# Revit family: BVFC gran
name_source: partatom
category: Modelos genéricos
revit_build: Autodesk Revit 2017 (Build: 20160225_1515(x64)
units: mm (PartAtom-declared; Revit-internal decimal feet)

## family parameters
Compartido = No
Corte con vacíos al cargar = No
Cota de conector redondo = Diámetro de uso
Puede alojar armadura = No
Punto de cálculo de habitación = No
Se basa en plano de trabajo = No
Siempre vertical = Sí
Tipo de pieza = Normal

## types (4) — shared parameters
EspPeu = 3 mm  [stored 0.00984252 ft]
F = 30 mm  [stored 0.0984252 ft]
Fabricante = Casals Ventilació
N = 100 mm  [stored 0.328084 ft]
Q = 60 mm  [stored 0.19685 ft]
T = 52 mm
URL = www.casals.com
a = 10 mm  [stored 0.0328084 ft]
b = 26 mm
esp = 2 mm  [stored 0.00656168 ft]

## per-type parameters (varying)
| type | A | B | C | Dimensiones | E | G | H | K | M | O | P |
| BVFC 20/20 | 1551 mm | 1118 mm | 1406 mm  [stored 4.61286 ft] | 1406x1217,5x1697 | 611 mm | 1300 mm  [stored 4.26509 ft] | 1013 mm | 1697 mm  [stored 5.56759 ft] | 1295 mm | 101 mm  [stored 0.331365 ft] | 407 mm |
| BVFC 22/22 | 1801 mm | 1202 mm | 1499 mm  [stored 4.91798 ft] | 1499x1301,5x1997 | 697 mm | 1393 mm  [stored 4.57021 ft] | 1097 mm | 1997 mm | 1388 mm  [stored 4.55381 ft] | 99 mm  [stored 0.324803 ft] | 406 mm  [stored 1.33202 ft] |
| BVFC 25/25 | 1901 mm | 1327 mm | 1709 mm  [stored 5.60696 ft] | 1709x1426,5x2097 | 793 mm  [stored 2.60171 ft] | 1603 mm  [stored 5.25919 ft] | 1222 mm  [stored 4.00919 ft] | 2048 mm | 1598 mm  [stored 5.24278 ft] | 101 mm  [stored 0.331365 ft] | 433 mm |
| BVFC 30/28 | 2108 mm | 1557 mm | 1906 mm | 1906x1656,5x2304 | 933 mm | 1800 mm  [stored 5.90551 ft] | 1452 mm  [stored 4.76378 ft] | 2304 mm | 1795 mm | 100 mm  [stored 0.328084 ft] | 524 mm  [stored 1.71916 ft] |

note: [stored X ft] marks values corroborated as IEEE doubles in the binary element streams (Revit-internal decimal feet)
